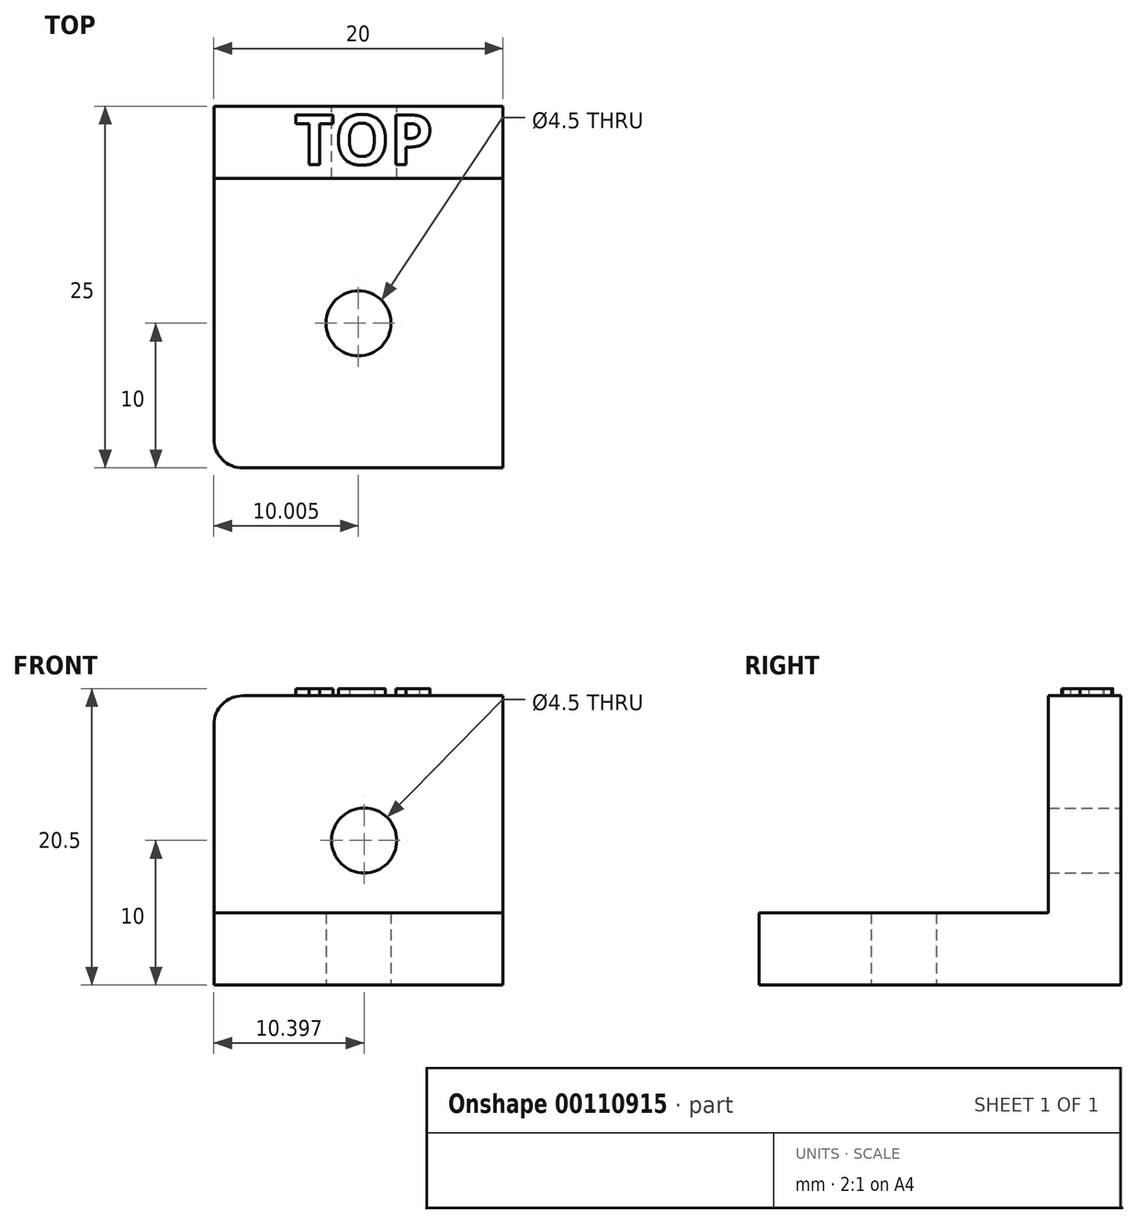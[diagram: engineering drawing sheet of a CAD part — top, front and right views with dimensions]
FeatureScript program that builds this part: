
annotation { "Feature Type Name" : "Feature", "Feature Type Description" : "" }
export const myFeature = defineFeature(function(context is Context, id is Id, definition is map)
    precondition{}
    {
        {
            var Q0;
            Q0=qCreatedBy(makeId("Top.planeOp"),FACE);
            var sketch = newSketch(context, id + "F0", { "sketchPlane" : qUnion([Q0])});
            skLineSegment(sketch, "E0.bottom", {"start": v(-9.66, 0) * mm, "end": v(10.34, 0) * mm});
            skLineSegment(sketch, "E0.top", {"start": v(-9.66, 25) * mm, "end": v(10.34, 25) * mm});
            skLineSegment(sketch, "E0.left", {"start": v(-9.66, 0) * mm, "end": v(-9.66, 25) * mm});
            skLineSegment(sketch, "E0.right", {"start": v(10.34, 0) * mm, "end": v(10.34, 25) * mm});
            skCircle(sketch, "E1", {"center": v(0.34, 10) * mm, "radius": 2.25 * mm});
            skPoint(sketch, "E2", {"position": v(0.34, 25) * mm});
            skPoint(sketch, "E3", {"position": v(-9.66, 10) * mm});
            skLineSegment(sketch, "E4", {"start": v(-9.66, 20) * mm, "end": v(10.34, 20) * mm});
            skSolve(sketch);
        }
        {
            var Q0;
            {var subQ1=sQuery(id+"F0.wireOp",EDGE,"E0.bottom");Q0=makeQuery(id+"F0.imprint","IMPRINT",FACE,{"disambiguationData":[TD([[makeQuery(id+"F0.imprint","IMPRINT",EDGE,{"derivedFrom":subQ1}),1.0]])]});}
            extrude(context, id + "F1", {"entities" : qUnion([Q0]), "depth" : 5 * mm});
        }
        {
            var Q0;
            {var subQ0=sQuery(id+"F0.wireOp",EDGE,"E0.top");Q0=makeQuery(id+"F0.imprint","IMPRINT",FACE,{"disambiguationData":[TD([[makeQuery(id+"F0.imprint","IMPRINT",EDGE,{"derivedFrom":subQ0}),-1.0]])]});}
            extrude(context, id + "F2", {"entities" : qUnion([Q0]), "operationType" : NewBodyOperationType.ADD, "depth" : 20 * mm});
        }
        {
            var Q0;
            Q0=makeQuery(id+"F2.opExtrude","CAP_EDGE",EDGE,{"disambiguationData":[OSD([sQuery(id+"F0.wireOp",EDGE,"E0.left")])],"isStart":false});
            var Q1;
            Q1=makeQuery(id+"F1.opExtrude","SWEPT_EDGE",EDGE,{"disambiguationData":[OSD([sQuery(id+"F0.wireOp",EDGE,"E0.bottom"),sQuery(id+"F0.wireOp",EDGE,"E0.left")])]});
            var Q2;
            Q2=makeQuery(id+"F1.opExtrude","CAP_EDGE",EDGE,{"disambiguationData":[OSD([sQuery(id+"F0.wireOp",EDGE,"E4")])],"isStart":false});
            fillet(context, id + "F3", {"entities" : qUnion([Q0, Q1, Q2]), "radius" : 2 * mm, "tangentPropagation" : true, "allowEdgeOverflow" : false});
        }
        {
            var Q0;
            Q0=makeQuery(id+"F2.opExtrude","SWEPT_FACE",FACE,{"disambiguationData":[OSD([sQuery(id+"F0.wireOp",EDGE,"E0.top")])]});
            var sketch = newSketch(context, id + "F4", { "sketchPlane" : qUnion([Q0])});
            skCircle(sketch, "E5", {"center": v(-0.74, 10) * mm, "radius": 2.25 * mm});
            skSolve(sketch);
        }
        {
            var Q0;
            Q0 = qSketchRegion(id + "F4", true);
            extrude(context, id + "F5", {"entities" : qUnion([Q0]), "operationType" : NewBodyOperationType.REMOVE, "oppositeDirection" : true, "depth" : 6 * mm});
        }
        {
            var Q0;
            Q0=makeQuery(id+"F2.opExtrude","CAP_FACE",FACE,{"disambiguationData":[OSD([sQuery(id+"F0.wireOp",EDGE,"E0.top"),sQuery(id+"F0.wireOp",EDGE,"E0.left"),sQuery(id+"F0.wireOp",EDGE,"E0.right"),sQuery(id+"F0.wireOp",EDGE,"E4")])],"isStart":false});
            var sketch = newSketch(context, id + "F6", { "sketchPlane" : qUnion([Q0])});
            skText(sketch, "E6", { "text": "TOP", "fontName": "OpenSans-Bold.ttf"});
            const initialGuessF6  = {"E6": [-0.0041, 0.02097, 1, 0, 0.00345]};
            skSetInitialGuess(sketch, initialGuessF6);
            skSolve(sketch);
        }
        {
            var Q0;
            Q0 = qSketchRegion(id + "F6", true);
            extrude(context, id + "F7", {"entities" : qUnion([Q0]), "operationType" : NewBodyOperationType.ADD, "depth" : 0.5 * mm});
        }
    });
